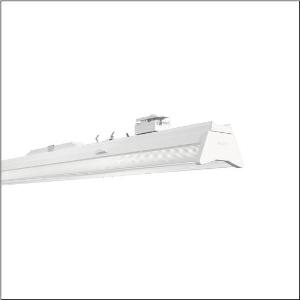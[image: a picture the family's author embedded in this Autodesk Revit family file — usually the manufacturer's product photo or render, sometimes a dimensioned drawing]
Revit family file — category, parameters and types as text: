
# Revit family: licross_r__11_performance_mo_51tm167n485g_4c90
name_source: partatom
category: Lighting Fixtures
units: mm (PartAtom-declared; Revit-internal decimal feet)

## family parameters
Cut with Voids When Loaded = No
Host = Face
Light Source = No
Part Type = Normal
Room Calculation Point = No
Round Connector Dimension = Use Diameter
Shared = No

## types (1)
- Licross® 11 Performance MO (1 x LED, 8840 lm, 48.6 W, 4000K)
    Apparent Load = 49 VA
    CIE Flux Codes = 66 88 96 79 100
    Color Rendering = 80
    Color Temperature = 4000K
    Default Elevation = 1800 mm
    Description = Licross® 11 Performance MO, luminaire insert, of sheet steel, galvanised, coil coated, white, length: 1.500mm, width: 120mm, height: 123mm, LED rated luminous flux: 8.840lm, light colour: 840, SDCM (Standard Deviation of Colour Matching)MacAdam ≤ 2 SDCM (initial), control gear: ON/OFF, with plug, 3-pole, with phase selection, mains connection: 220..240V, AC, 50/60Hz, rated input power: 49W, internal wiring halogen-free, primary light control with lens, of plastic, primary optical cover: cover, of PMMA, light emission: direct/indirect distribution, primary light characteristic: symmetric, protection rating (complete): IP40, insulation class (complete): insulation class I (protective earthing), certification: CE, ENEC, VDE, UKCA, protection symbol: D if used in an environment without relevant dust loads with corresponding accessories, impact resistance: IK06, permissible ambient temperature for indoor applications: -25..+35°C, corresponds to IFS (International Featured Standards) requirements for safety and quality in the food industry, reducing of maximum allowable ambient temperature of 5°C with ceiling mounting, LABS conformity tested according to VDMA 24364:2018-05, packaging unit: 1 piece
    Height = 114 mm
    Lamp = 1 x LED
    Lamp Light Flux = 8840 lm
    Lamp Power = 48.6 W
    Lamp count = 1
    Length = 1500 mm
    Luminous efficacy = 182 lm/W
    Manufacturer = Siteco
    ModVariant = No
    Model = 51TM167N485G
    Mounting Place = Ceiling
    Mounting Type = Pendant
    Number of Poles = 1
    OnlyDefault = Yes
    Power Factor = 1
    Product Name = Licross® 11 Performance MO
    Product group = luminaire insert | ceiling pendant
    ProductGroupID = 901
    Protection Class = Protection class I
    Protection Degree = IP 40
    RLX_Detail_Level = 1
    RLX_Emergency_Light_Flux = 0 lm
    RLX_Emergency_Type = 0
    RLX_Emergency_Type_DB = No
    RlxData = <blob elided: 30569 chars, md5=df8da80d>
    Socket = socket
    Standby Power = 0 W
    System Light Flux = 8840 lm
    System Power = 49 W
    Type Comments = Product without accessories
    Type Image = l_1256138.jpg
    URL = http://relux.com
    VarID = ---
    Voltage = 0 V
    Weight = 0.00 kg
    Width = 120 mm

## geometry (parser evidence)
native form markers: Blend x4, Sweep x12
no freeform markers — native parametric forms only
